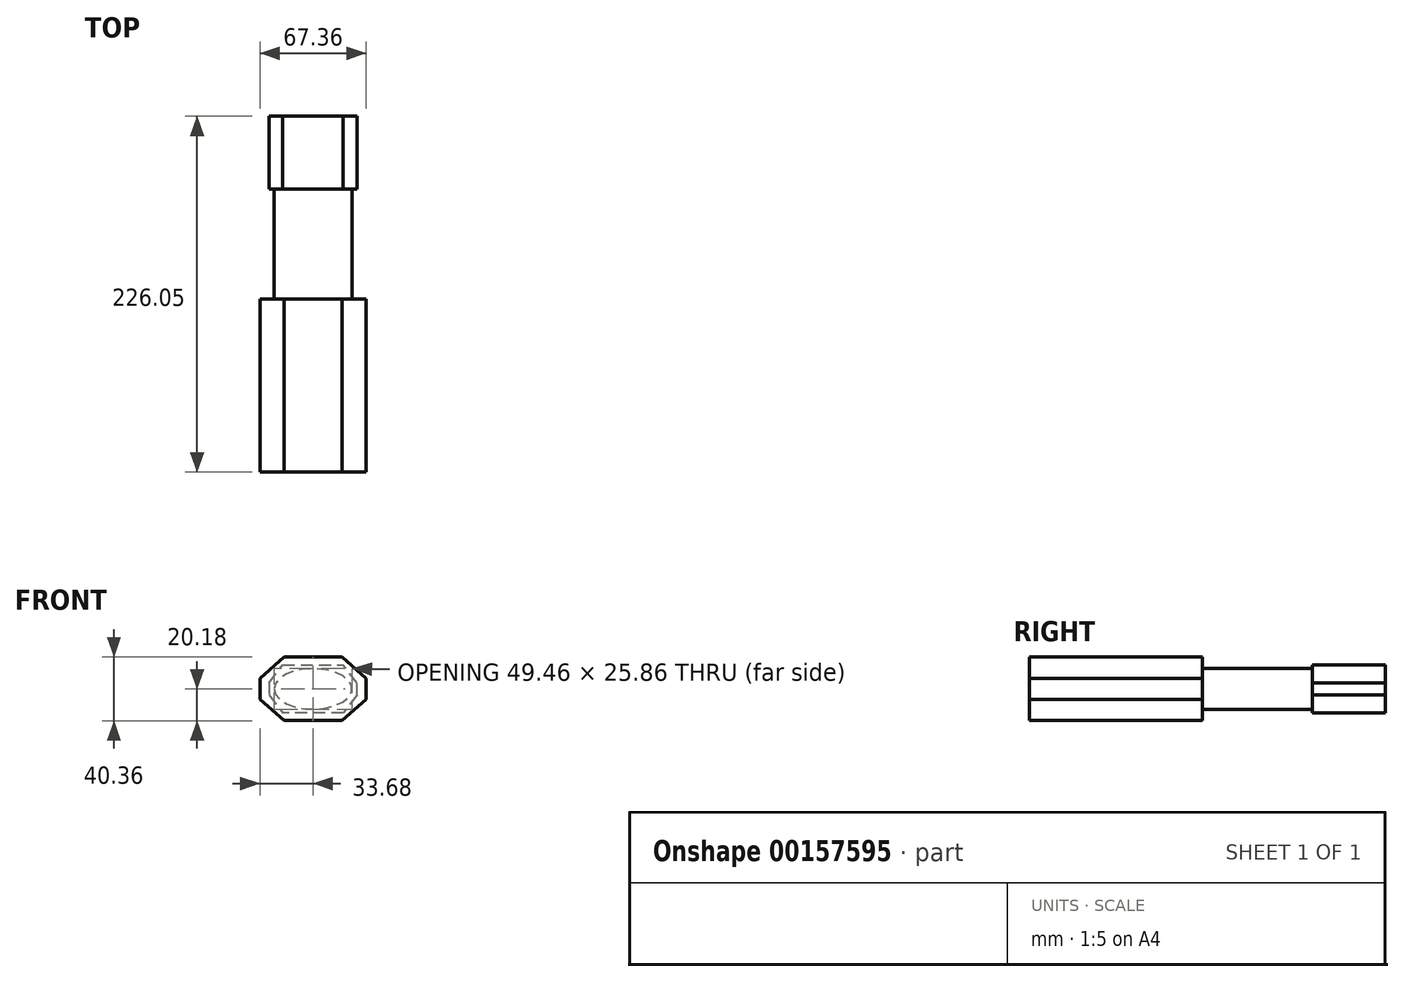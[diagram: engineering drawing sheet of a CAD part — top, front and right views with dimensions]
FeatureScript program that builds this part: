
annotation { "Feature Type Name" : "Feature", "Feature Type Description" : "" }
export const myFeature = defineFeature(function(context is Context, id is Id, definition is map)
    precondition{}
    {
        {
            var Q0;
            Q0=qCreatedBy(makeId("Front.planeOp"),FACE);
            var sketch = newSketch(context, id + "F0", { "sketchPlane" : qUnion([Q0])});
            skLineSegment(sketch, "E0", {"start": v(-18.3, 20.18) * mm, "end": v(-33.68, 6.72) * mm});
            skLineSegment(sketch, "E1.MirrorCS", {"start": v(18.3, 20.18) * mm, "end": v(33.68, 6.72) * mm});
            skLineSegment(sketch, "E2.MirrorCS", {"start": v(-18.3, -20.18) * mm, "end": v(-33.68, -6.72) * mm});
            skLineSegment(sketch, "E3.MirrorCS", {"start": v(18.3, -20.18) * mm, "end": v(33.68, -6.72) * mm});
            skLineSegment(sketch, "E4", {"start": v(-18.3, 20.18) * mm, "end": v(18.3, 20.18) * mm});
            skLineSegment(sketch, "E5", {"start": v(33.68, 6.72) * mm, "end": v(33.68, -6.72) * mm});
            skLineSegment(sketch, "E6", {"start": v(-33.68, -6.72) * mm, "end": v(-33.68, 6.72) * mm});
            skLineSegment(sketch, "E7", {"start": v(-18.3, -20.18) * mm, "end": v(18.3, -20.18) * mm});
            skSolve(sketch);
        }
        {
            var Q0;
            Q0=qCreatedBy(makeId("Front.planeOp"),FACE);
            var sketch = newSketch(context, id + "F1", { "sketchPlane" : qUnion([Q0])});
            skEllipse(sketch, "E8", {"center": v(0, 0) * mm, "majorRadius": 12.93 * mm, "minorRadius": 24.73 * mm, "majorAxis": v(0, 1)});
            skSolve(sketch);
        }
        {
            var Q0;
            Q0=makeQuery(id+"F0.imprint","IMPRINT",FACE,{"disambiguationData":[TD([[makeQuery(id+"F0.imprint","IMPRINT",EDGE,{"derivedFrom":sQuery(id+"F0.wireOp",EDGE,"E0")}),1.0]])]});
            extrude(context, id + "F2", {"entities" : qUnion([Q0]), "depth" : 109.85 * mm});
        }
        {
            var Q0;
            Q0 = qSketchRegion(id + "F1", true);
            extrude(context, id + "F3", {"entities" : qUnion([Q0]), "operationType" : NewBodyOperationType.ADD, "oppositeDirection" : true, "depth" : 69.85 * mm});
        }
        {
            var Q0;
            Q0=makeQuery(id+"F3.opExtrude","CAP_FACE",FACE,{"disambiguationData":[OSD([sQuery(id+"F1.wireOp",EDGE,"E8")])],"isStart":false});
            cPlane(context, id + "F4", {"entities" : qUnion([Q0]), "cplaneType" : CPlaneType.OFFSET, "offset" : 0 * mm, "oppositeDirection" : true, "width" : 152.4 * mm, "height" : 152.4 * mm});
        }
        {
            var Q0;
            Q0=qCreatedBy(id+"F4.planeOp",FACE);
            var sketch = newSketch(context, id + "F5", { "sketchPlane" : qUnion([Q0])});
            skLineSegment(sketch, "E9", {"start": v(-27.88, 0) * mm, "end": v(-27.88, 3.92) * mm});
            skLineSegment(sketch, "E10", {"start": v(-27.88, 3.92) * mm, "end": v(-19.17, 15.25) * mm});
            skLineSegment(sketch, "E11", {"start": v(-19.17, 15.25) * mm, "end": v(0, 15.25) * mm});
            skLineSegment(sketch, "E12.MirrorCS", {"start": v(27.88, 3.92) * mm, "end": v(19.17, 15.25) * mm});
            skLineSegment(sketch, "E13.MirrorCS", {"start": v(19.17, 15.25) * mm, "end": v(0, 15.25) * mm});
            skLineSegment(sketch, "E14.MirrorCS", {"start": v(-27.88, -3.92) * mm, "end": v(-19.17, -15.25) * mm});
            skLineSegment(sketch, "E15.MirrorCS", {"start": v(-19.17, -15.25) * mm, "end": v(0, -15.25) * mm});
            skLineSegment(sketch, "E16.MirrorCS", {"start": v(19.17, -15.25) * mm, "end": v(0, -15.25) * mm});
            skLineSegment(sketch, "E17.MirrorCS", {"start": v(27.88, -3.92) * mm, "end": v(19.17, -15.25) * mm});
            skLineSegment(sketch, "E18", {"start": v(-27.88, -3.92) * mm, "end": v(-27.88, 0) * mm});
            skLineSegment(sketch, "E19", {"start": v(27.88, 3.92) * mm, "end": v(27.88, -3.92) * mm});
            skSolve(sketch);
        }
        {
            var Q0;
            Q0=makeQuery(id+"F5.imprint","IMPRINT",FACE,{"disambiguationData":[TD([[makeQuery(id+"F5.imprint","IMPRINT",EDGE,{"derivedFrom":sQuery(id+"F5.wireOp",EDGE,"E9")}),-1.0]])]});
            extrude(context, id + "F6", {"entities" : qUnion([Q0]), "operationType" : NewBodyOperationType.ADD, "depth" : 46.35 * mm});
        }
    });
